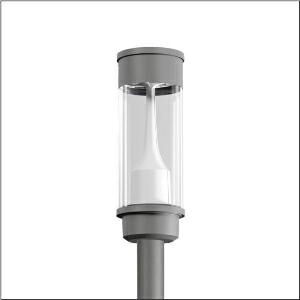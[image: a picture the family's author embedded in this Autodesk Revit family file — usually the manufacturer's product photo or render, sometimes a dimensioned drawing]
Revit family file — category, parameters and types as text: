
# Revit family: litepole_iq___st1_2a_5xa5415af14h_245c
name_source: partatom
category: Lighting Fixtures
units: mm (PartAtom-declared; Revit-internal decimal feet)

## family parameters
Cut with Voids When Loaded = No
Host = Face
Light Source = No
Part Type = Normal
Room Calculation Point = No
Round Connector Dimension = Use Diameter
Shared = No

## types (1)
- --- (1 x LED, 1540 lm, 12.9 W, 2200K)
    Apparent Load = 13 VA
    CIE Flux Codes = 22 61 93 96 100
    Color Rendering = 70
    Color Temperature = 2200K
    Default Elevation = 1800 mm
    Description = Litepole iQ, mast luminaire, Module 540 iQ-SR, primary light control with 3 zone facetted reflector, of plastic, silver coated, highly specular, structured, primary optical cover: cover, of PMMA, transparent, partly coated, light distribution: ST1.2a, light emission: direct distribution, primary light characteristic: asymmetric, installation type: post-top, LED, High Power LED, rated luminous flux: 1.540lm, luminous efficacy: 119lm/W, light colour: 722, colour temperature: 2200K, control gear: ECG iQ, control: optimised constant luminous flux control (CLO 2.0), Desk-Remote (wireless, voltage-free reading and setting of iQ features in the workshop via application-optimized NFC function/RFID function), Light-Fading, Smart-Wire, Night-Set, Lumen-Switch, Temp-Guard, Auto-Match, Street-Remote, presetting dimming logarithmic, with terminal, 6-pole, max. 2.5mm², mains connection: 230..240V, AC, 50/60Hz, start of lifetime: 13W, end of service life: 13W, reduction: 6W, luminaire housing, upper part, of glass-fibre reinforced polyester, coated, Siteco® metallic grey (DB 702S), diameter: 210mm, height: 590mm, spigot size: d x l = 76 x 70mm (post-top) | with reducer (optional accessory) 60 x 70mm, post-top mast mounting element, of diecast aluminium, coated, Siteco® metallic grey (DB 702S), Module 540 iQ-SR, traffic white (RAL 9016), equipment: standard, protection rating (complete): IP65, insulation class (complete): insulation class II (safety insulation), certification: CE, ENEC, VDE, packaging unit: 1 piece

Light Distribution: ST1.2a
    Height = 590 mm
    Lamp = 1 x LED
    Lamp Light Flux = 1540 lm
    Lamp Power = 12.9 W
    Lamp count = 1
    Length = 220 mm
    Luminous efficacy = 119 lm/W
    Manufacturer = Siteco
    ModVariant = No
    Model = 5XA5415AF14H
    Number of Poles = 1
    OnlyDefault = Yes
    Power Factor = 1
    Product Name = Litepole iQ | ST1.2a
    Product group = mast luminaire | pylon top
    ProductGroupID = 6100
    Protection Class = Protection class II
    Protection Degree = IP 65
    RLX_Detail_Level = 1
    RLX_Emergency_Light_Flux = 0 lm
    RLX_Emergency_Type = 0
    RLX_Emergency_Type_DB = No
    RlxData = <blob elided: 72505 chars, md5=218aefc2>
    Socket = socket
    Standby Power = 0 W
    System Light Flux = 1540 lm
    System Power = 13 W
    Type Comments = factory setting: luminous flux: 100 % | dim-lin: 254 | 516 mA
    Type Image = l_1006025.jpg
    URL = http://relux.com
    VarID = @adj_109067
    Voltage = 0 V
    Weight = 0.00 kg
    Width = 0 mm  [stored 0 ft]

note: [stored X ft] marks values corroborated as IEEE doubles in the binary element streams (Revit-internal decimal feet)

## geometry (parser evidence)
native form markers: Blend x4, Sweep x9
no freeform markers — native parametric forms only
